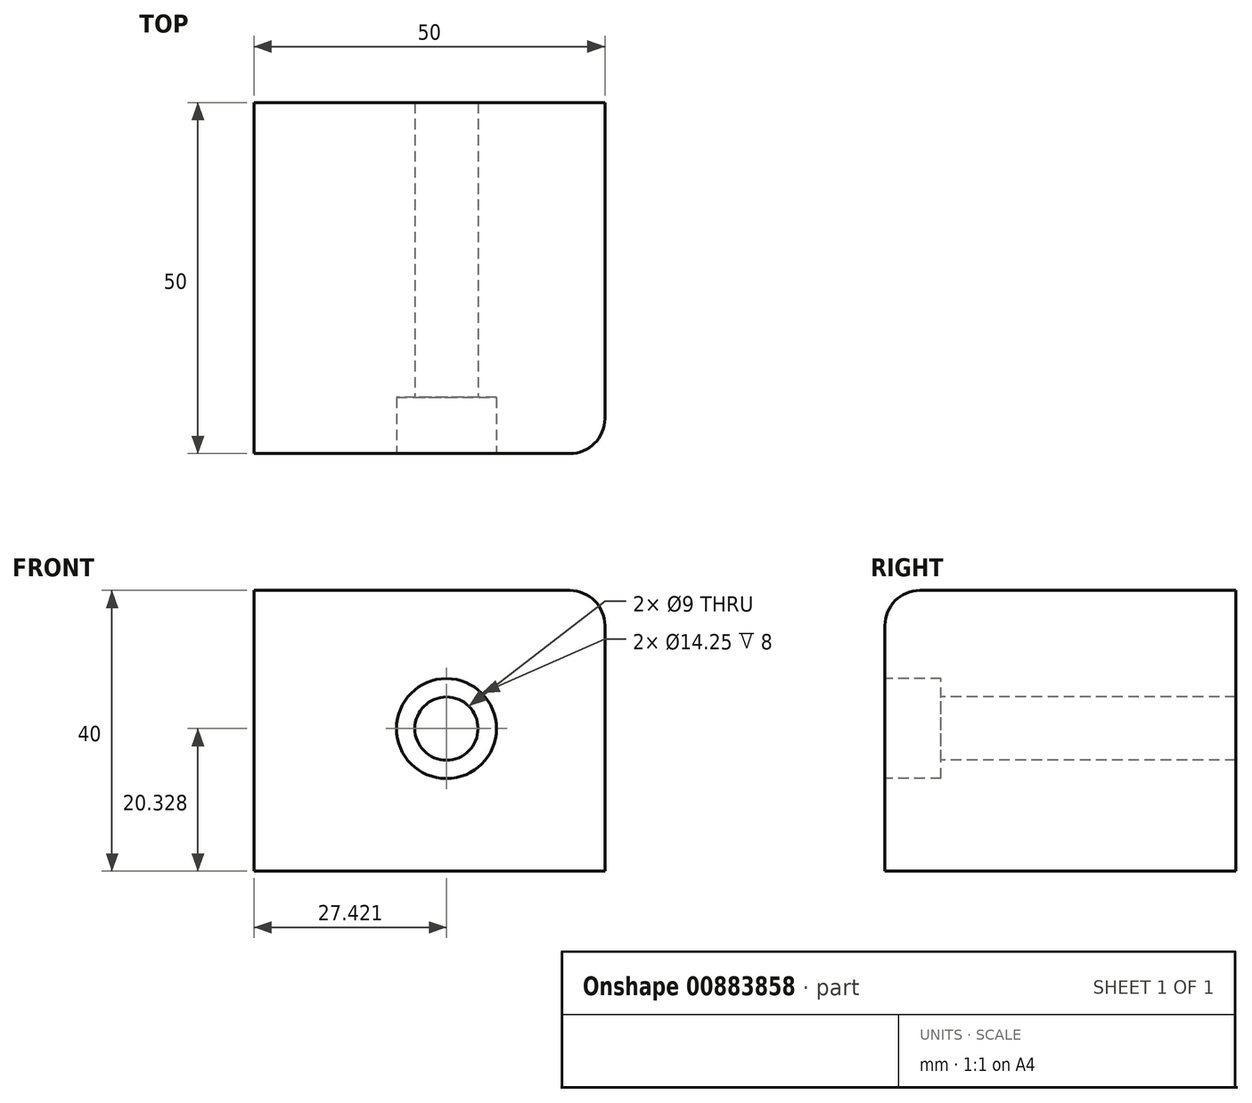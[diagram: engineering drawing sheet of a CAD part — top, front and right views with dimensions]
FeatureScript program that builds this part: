
annotation { "Feature Type Name" : "Feature", "Feature Type Description" : "" }
export const myFeature = defineFeature(function(context is Context, id is Id, definition is map)
    precondition{}
    {
        {
            var Q0;
            Q0=qCreatedBy(makeId("Front.planeOp"),FACE);
            var sketch = newSketch(context, id + "F0", { "sketchPlane" : qUnion([Q0])});
            skLineSegment(sketch, "E0.bottom", {"start": v(0, 0) * mm, "end": v(50, 0) * mm});
            skLineSegment(sketch, "E0.top", {"start": v(0, 40) * mm, "end": v(50, 40) * mm});
            skLineSegment(sketch, "E0.left", {"start": v(0, 0) * mm, "end": v(0, 40) * mm});
            skLineSegment(sketch, "E0.right", {"start": v(50, 0) * mm, "end": v(50, 40) * mm});
            skSolve(sketch);
        }
        {
            var Q0;
            Q0 = qSketchRegion(id + "F0", true);
            extrude(context, id + "F1", {"entities" : qUnion([Q0]), "depth" : 50 * mm, "offsetDistance" : 25 * mm});
        }
        {
            var Q0;
            Q0=makeQuery(id+"F1.opExtrude","CAP_FACE",FACE,{"disambiguationData":[OSD([sQuery(id+"F0.wireOp",EDGE,"E0.bottom"),sQuery(id+"F0.wireOp",EDGE,"E0.top"),sQuery(id+"F0.wireOp",EDGE,"E0.left"),sQuery(id+"F0.wireOp",EDGE,"E0.right")])],"isStart":false});
            var sketch = newSketch(context, id + "F2", { "sketchPlane" : qUnion([Q0])});
            skPoint(sketch, "E1", {"position": v(27.42, 20.33) * mm});
            skSolve(sketch);
        }
        {
            var Q0;
            Q0=sQuery(id+"F2.wireOp",VERTEX,"E1");
            var Q1;
            Q1=makeQuery(id+"F1.opExtrude","SWEPT_BODY",BODY,{"disambiguationData":[OSD([sQuery(id+"F0.wireOp",EDGE,"E0.bottom"),sQuery(id+"F0.wireOp",EDGE,"E0.top"),sQuery(id+"F0.wireOp",EDGE,"E0.left"),sQuery(id+"F0.wireOp",EDGE,"E0.right")])]});
            hole(context, id + "F3", {"style" : HoleStyle.C_BORE, "endStyle" : HoleEndStyle.THROUGH, "standardTappedOrClearance" : lookupTablePath({ "fit" : "Normal", "standard" : "ISO", "size" : "M8", "type" : "Clearance" }), "standardBlindInLast" : lookupTablePath({ "fit" : "Normal", "standard" : "ISO", "engagement" : "75%", "pitch" : "1.25 mm", "size" : "M8", "type" : "Clearance & tapped" }), "holeDiameter" : 9 * mm, "cBoreDiameter" : 14.25 * mm, "cBoreDepth" : 8 * mm, "majorDiameter" : 5 * mm, "isTappedThrough" : true, "tappedDepth" : 12 * mm, "tapClearance" : 3, "startFromSketch" : true, "locations" : qUnion([Q0]), "scope" : qUnion([Q1])});
        }
        {
            var Q0;
            Q0=makeQuery(id+"F1.opExtrude","CAP_EDGE",EDGE,{"disambiguationData":[OSD([sQuery(id+"F0.wireOp",EDGE,"E0.top")])],"isStart":false});
            var Q1;
            Q1=makeQuery(id+"F1.opExtrude","CAP_EDGE",EDGE,{"disambiguationData":[OSD([sQuery(id+"F0.wireOp",EDGE,"E0.right")])],"isStart":false});
            var Q2;
            Q2=makeQuery(id+"F1.opExtrude","SWEPT_EDGE",EDGE,{"disambiguationData":[OSD([sQuery(id+"F0.wireOp",EDGE,"E0.top"),sQuery(id+"F0.wireOp",EDGE,"E0.right")])]});
            fillet(context, id + "F4", {"entities" : qUnion([Q0, Q1, Q2]), "tangentPropagation" : true, "radius" : 5 * mm, "defaultsChanged" : false, "vertexSettings" : [], "allowEdgeOverflow" : false});
        }
    });
